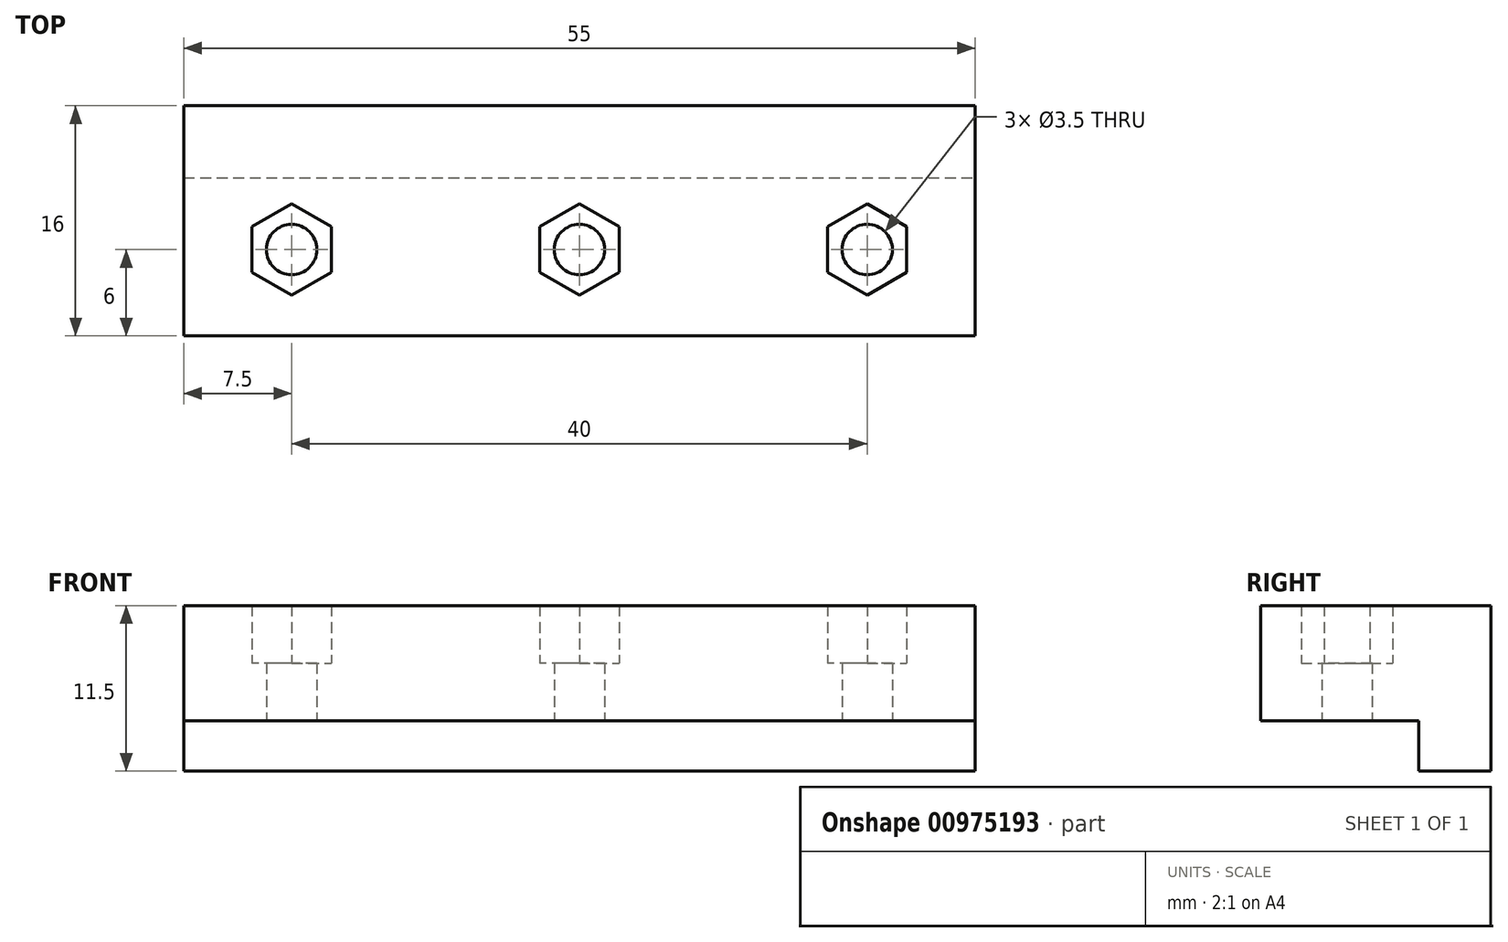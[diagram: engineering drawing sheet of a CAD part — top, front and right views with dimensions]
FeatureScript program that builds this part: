
annotation { "Feature Type Name" : "Feature", "Feature Type Description" : "" }
export const myFeature = defineFeature(function(context is Context, id is Id, definition is map)
    precondition{}
    {
        {
            var Q0;
            Q0=qCreatedBy(makeId("Top.planeOp"),FACE);
            var sketch = newSketch(context, id + "F0", { "sketchPlane" : qUnion([Q0])});
            skLineSegment(sketch, "E0.bottom", {"start": v(-27.5, 8) * mm, "end": v(27.5, 8) * mm});
            skLineSegment(sketch, "E0.top", {"start": v(-27.5, -8) * mm, "end": v(27.5, -8) * mm});
            skLineSegment(sketch, "E0.left", {"start": v(-27.5, 8) * mm, "end": v(-27.5, -8) * mm});
            skLineSegment(sketch, "E0.right", {"start": v(27.5, 8) * mm, "end": v(27.5, -8) * mm});
            skPoint(sketch, "E0.middle", {"position": v(0, 0) * mm});
            skLineSegment(sketch, "E1", {"start": v(-27.5, 3) * mm, "end": v(27.5, 3) * mm});
            skCircle(sketch, "E2.cCircle", {"center": v(0, -2) * mm, "radius": 2.75 * mm, "construction": true});
            skLineSegment(sketch, "E2.0", {"start": v(-2.75, -3.59) * mm, "end": v(-2.75, -0.41) * mm});
            skLineSegment(sketch, "E2.1", {"start": v(-2.75, -0.41) * mm, "end": v(0, 1.18) * mm});
            skLineSegment(sketch, "E2.2", {"start": v(0, 1.18) * mm, "end": v(2.75, -0.41) * mm});
            skLineSegment(sketch, "E2.3", {"start": v(2.75, -0.41) * mm, "end": v(2.75, -3.59) * mm});
            skLineSegment(sketch, "E2.4", {"start": v(2.75, -3.59) * mm, "end": v(0, -5.18) * mm});
            skLineSegment(sketch, "E2.5", {"start": v(0, -5.18) * mm, "end": v(-2.75, -3.59) * mm});
            skPoint(sketch, "E2.0.midPoint", {"position": v(-2.75, -2) * mm});
            skCircle(sketch, "E3", {"center": v(0, -2) * mm, "radius": 1.75 * mm});
            skCircle(sketch, "E4.cCircle", {"center": v(-20, -2) * mm, "radius": 2.75 * mm, "construction": true});
            skLineSegment(sketch, "E4.0", {"start": v(-22.75, -3.59) * mm, "end": v(-22.75, -0.41) * mm});
            skLineSegment(sketch, "E4.1", {"start": v(-22.75, -0.41) * mm, "end": v(-20, 1.18) * mm});
            skLineSegment(sketch, "E4.2", {"start": v(-20, 1.18) * mm, "end": v(-17.25, -0.41) * mm});
            skLineSegment(sketch, "E4.3", {"start": v(-17.25, -0.41) * mm, "end": v(-17.25, -3.59) * mm});
            skLineSegment(sketch, "E4.4", {"start": v(-17.25, -3.59) * mm, "end": v(-20, -5.18) * mm});
            skLineSegment(sketch, "E4.5", {"start": v(-20, -5.18) * mm, "end": v(-22.75, -3.59) * mm});
            skPoint(sketch, "E4.0.midPoint", {"position": v(-22.75, -2) * mm});
            skCircle(sketch, "E5", {"center": v(-20, -2) * mm, "radius": 1.75 * mm});
            skCircle(sketch, "E6.cCircle", {"center": v(20, -2) * mm, "radius": 2.75 * mm, "construction": true});
            skLineSegment(sketch, "E6.0", {"start": v(22.75, -0.41) * mm, "end": v(22.75, -3.59) * mm});
            skLineSegment(sketch, "E6.1", {"start": v(22.75, -3.59) * mm, "end": v(20, -5.18) * mm});
            skLineSegment(sketch, "E6.2", {"start": v(20, -5.18) * mm, "end": v(17.25, -3.59) * mm});
            skLineSegment(sketch, "E6.3", {"start": v(17.25, -3.59) * mm, "end": v(17.25, -0.41) * mm});
            skLineSegment(sketch, "E6.4", {"start": v(17.25, -0.41) * mm, "end": v(20, 1.18) * mm});
            skLineSegment(sketch, "E6.5", {"start": v(20, 1.18) * mm, "end": v(22.75, -0.41) * mm});
            skPoint(sketch, "E6.0.midPoint", {"position": v(22.75, -2) * mm});
            skCircle(sketch, "E7", {"center": v(20, -2) * mm, "radius": 1.75 * mm});
            skSolve(sketch);
        }
        {
            var Q0;
            {var subQ0=sQuery(id+"F0.wireOp",EDGE,"E0.bottom");Q0=makeQuery(id+"F0.imprint","IMPRINT",FACE,{"disambiguationData":[TD([[makeQuery(id+"F0.imprint","IMPRINT",EDGE,{"derivedFrom":subQ0}),-1.0]])]});}
            var Q1;
            {var subQ0=sQuery(id+"F0.wireOp",EDGE,"E0.top");Q1=makeQuery(id+"F0.imprint","IMPRINT",FACE,{"disambiguationData":[TD([[makeQuery(id+"F0.imprint","IMPRINT",EDGE,{"derivedFrom":subQ0}),1.0]])]});}
            extrude(context, id + "F1", {"entities" : qUnion([Q0, Q1]), "depth" : 8 * mm, "offsetDistance" : 25 * mm});
        }
        {
            var Q0;
            Q0=makeQuery(id+"F0.imprint","IMPRINT",FACE,{"disambiguationData":[TD([[makeQuery(id+"F0.imprint","IMPRINT",EDGE,{"derivedFrom":sQuery(id+"F0.wireOp",EDGE,"E4.0")}),-1.0]])]});
            var Q1;
            Q1=makeQuery(id+"F0.imprint","IMPRINT",FACE,{"disambiguationData":[TD([[makeQuery(id+"F0.imprint","IMPRINT",EDGE,{"derivedFrom":sQuery(id+"F0.wireOp",EDGE,"E2.0")}),-1.0]])]});
            var Q2;
            Q2=makeQuery(id+"F0.imprint","IMPRINT",FACE,{"disambiguationData":[TD([[makeQuery(id+"F0.imprint","IMPRINT",EDGE,{"derivedFrom":sQuery(id+"F0.wireOp",EDGE,"E6.0")}),-1.0]])]});
            extrude(context, id + "F2", {"entities" : qUnion([Q0, Q1, Q2]), "operationType" : NewBodyOperationType.ADD, "depth" : 4 * mm, "offsetDistance" : 25 * mm});
        }
        {
            var Q0;
            {var subQ0=sQuery(id+"F0.wireOp",EDGE,"E0.bottom");Q0=makeQuery(id+"F0.imprint","IMPRINT",FACE,{"disambiguationData":[TD([[makeQuery(id+"F0.imprint","IMPRINT",EDGE,{"derivedFrom":subQ0}),-1.0]])]});}
            extrude(context, id + "F3", {"entities" : qUnion([Q0]), "operationType" : NewBodyOperationType.ADD, "oppositeDirection" : true, "depth" : 3.5 * mm, "offsetDistance" : 25 * mm});
        }
    });
